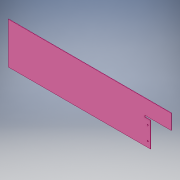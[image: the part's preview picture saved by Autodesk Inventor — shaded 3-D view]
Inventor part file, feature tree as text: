
AUTODESK INVENTOR PART (.ipt)
format: ipt  version: 2018 (Build 220112000, 112)  size: 117,248 bytes
history: native  units: mm
features: extrude x3, sketch x3
ambient origin geometry x8: Origin, YZ Plane, XZ Plane, XY Plane, X Axis, Y Axis, Z Axis, Center Point
bodies: Solid1 (feature_tree)
feature tree (6):
  extrude  "Extrusion1"  Depth=150.0mm
  extrude  "Extrusion3"  Depth=20.0mm
  extrude  "Extrusion4"  Depth=95.0mm
  sketch  "Sketch1"  dims[d0=515.0mm d1=150.0mm]
  sketch  "Sketch2"  dims[d2=1.6mm d3=0.0mm d6=20.0mm]
  sketch  "Sketch3"  dims[d7=60.0mm d10=5.0mm d11=5.0mm d12=50.0mm d13=20.0mm d14=1.6mm d15=0.0mm d16=54.0mm d17=1.6mm d18=95.0mm d19=0.0mm]
